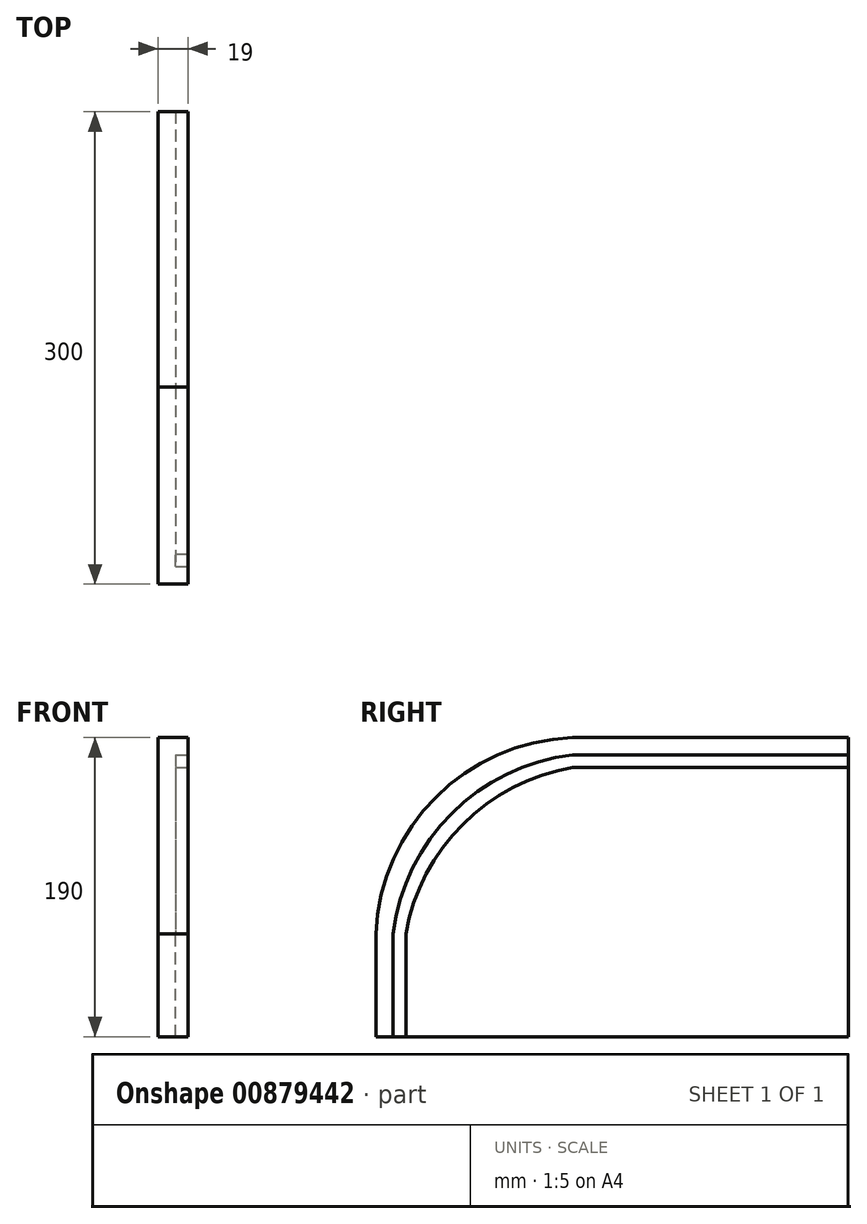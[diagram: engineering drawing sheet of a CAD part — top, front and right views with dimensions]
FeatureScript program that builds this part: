
annotation { "Feature Type Name" : "Feature", "Feature Type Description" : "" }
export const myFeature = defineFeature(function(context is Context, id is Id, definition is map)
    precondition{}
    {
        {
            var Q0;
            Q0=qCreatedBy(makeId("Right.planeOp"),FACE);
            var sketch = newSketch(context, id + "F0", { "sketchPlane" : qUnion([Q0])});
            skLineSegment(sketch, "E0.bottom", {"start": v(-25, 95) * mm, "end": v(150, 95) * mm});
            skLineSegment(sketch, "E0.top", {"start": v(-150, -95) * mm, "end": v(150, -95) * mm});
            skLineSegment(sketch, "E0.left", {"start": v(-150, -29.82) * mm, "end": v(-150, -95) * mm});
            skLineSegment(sketch, "E0.right", {"start": v(150, 95) * mm, "end": v(150, -95) * mm});
            skPoint(sketch, "E0.middle", {"position": v(0, 0) * mm});
            skPoint(sketch, "E1", {"position": v(-150, -40) * mm});
            skPoint(sketch, "E2", {"position": v(-25, 95) * mm});
            skArc(sketch, "E3", {"start": v(-25, 95) * mm, "mid": v(-115.49, 53.42) * mm, "end": v(-150, -40) * mm});
            skPoint(sketch, "E4.orphan", {"position": v(-150, 95) * mm});
            skSolve(sketch);
        }
        {
            var Q0;
            {var subQ5=sQuery(id+"F0.wireOp",EDGE,"E0.bottom");Q0=makeQuery(id+"F0.imprint","IMPRINT",FACE,{"disambiguationData":[TD([[makeQuery(id+"F0.imprint","IMPRINT",EDGE,{"derivedFrom":subQ5}),-1.0]])]});}
            extrude(context, id + "F1", {"entities" : qUnion([Q0]), "flatOperationType" : FlatOperationType.REMOVE, "depth" : 19 * mm, "offsetDistance" : 25 * mm, "domain" : OperationDomain.MODEL});
        }
        {
            var Q0;
            Q0=makeQuery(id+"F1.opExtrude","CAP_FACE",FACE,{"disambiguationData":[OSD([sQuery(id+"F0.wireOp",EDGE,"E0.bottom"),sQuery(id+"F0.wireOp",EDGE,"E0.top"),sQuery(id+"F0.wireOp",EDGE,"E0.left"),sQuery(id+"F0.wireOp",EDGE,"E0.right"),sQuery(id+"F0.wireOp",EDGE,"E3")])],"isStart":false});
            var sketch = newSketch(context, id + "F2", { "sketchPlane" : qUnion([Q0])});
            skPoint(sketch, "E5", {"position": v(150, 84) * mm});
            skPoint(sketch, "E6", {"position": v(150, 76) * mm});
            skLineSegment(sketch, "E7", {"start": v(150, 84) * mm, "end": v(-25, 84) * mm});
            skLineSegment(sketch, "E8", {"start": v(150, 76) * mm, "end": v(-25, 76) * mm});
            skPoint(sketch, "E9", {"position": v(-139, -95) * mm});
            skPoint(sketch, "E10", {"position": v(-131, -95) * mm});
            skLineSegment(sketch, "E11", {"start": v(-139, -95) * mm, "end": v(-139, -29.82) * mm});
            skLineSegment(sketch, "E12", {"start": v(-131, -95) * mm, "end": v(-131, -29.82) * mm});
            skArc(sketch, "E13", {"start": v(-25, 76) * mm, "mid": v(-94.77, 39.9) * mm, "end": v(-131, -29.82) * mm});
            skArc(sketch, "E14", {"start": v(-25, 84) * mm, "mid": v(-101.75, 46.88) * mm, "end": v(-139, -29.82) * mm});
            skSolve(sketch);
        }
        {
            var Q0;
            {var subQ1=sQuery(id+"F2.wireOp",EDGE,"E7");Q0=makeQuery(id+"F2.imprint","IMPRINT",FACE,{"disambiguationData":[TD([[makeQuery(id+"F2.imprint","IMPRINT",EDGE,{"derivedFrom":subQ1}),1.0]])]});}
            extrude(context, id + "F3", {"entities" : qUnion([Q0]), "operationType" : NewBodyOperationType.REMOVE, "flatOperationType" : FlatOperationType.REMOVE, "oppositeDirection" : true, "depth" : 8 * mm, "offsetDistance" : 25 * mm, "domain" : OperationDomain.MODEL});
        }
    });
